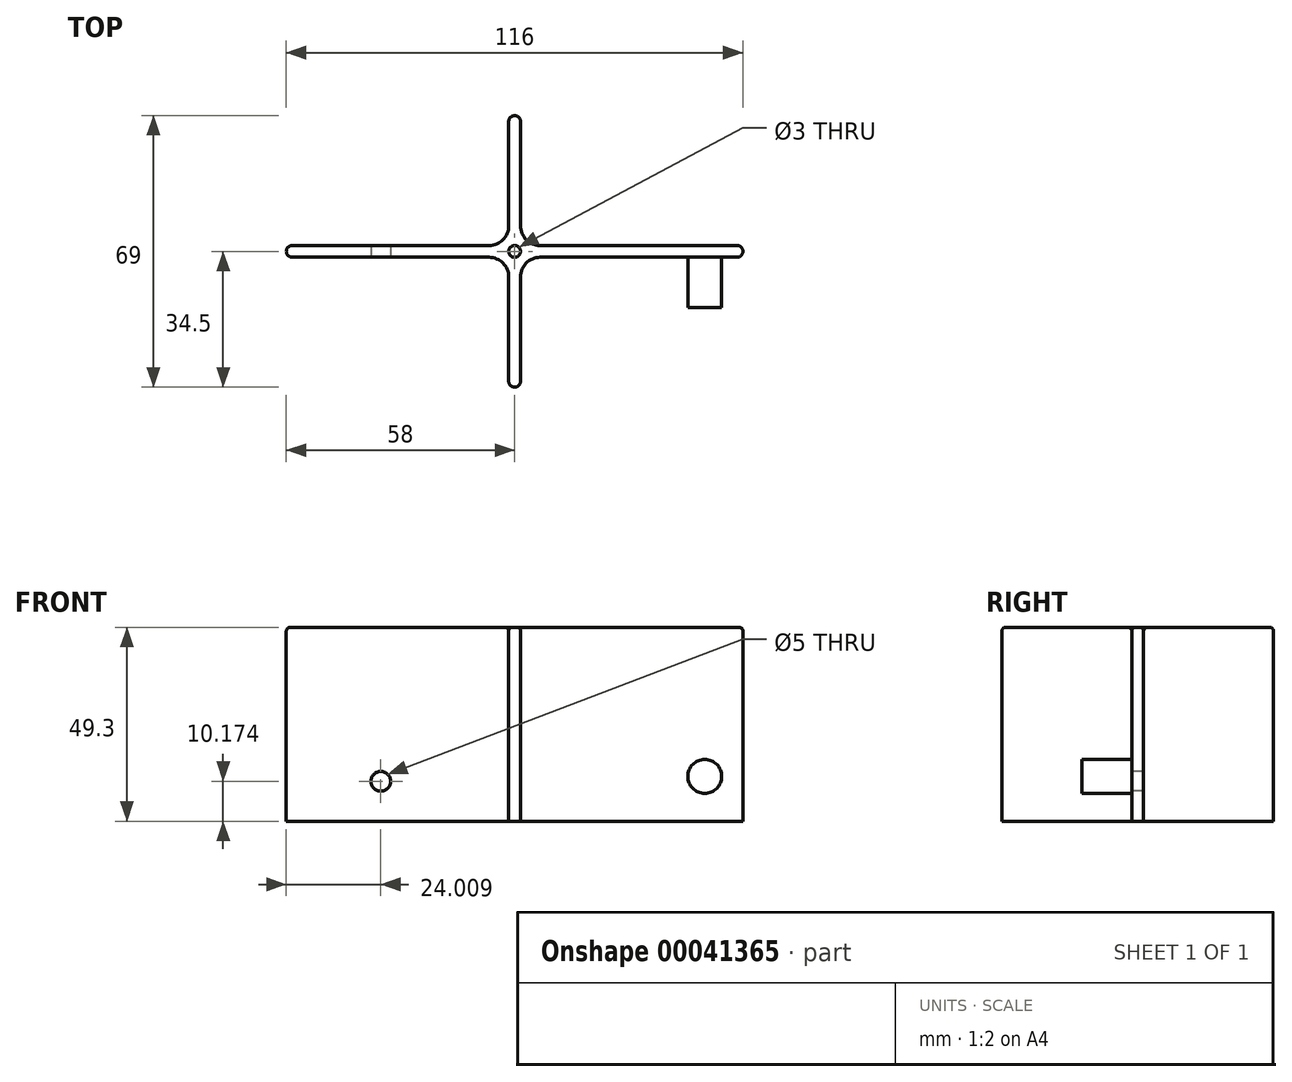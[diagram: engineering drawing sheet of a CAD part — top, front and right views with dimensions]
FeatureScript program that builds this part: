
annotation { "Feature Type Name" : "Feature", "Feature Type Description" : "" }
export const myFeature = defineFeature(function(context is Context, id is Id, definition is map)
    precondition{}
    {
        {
            var Q0;
            Q0=qCreatedBy(makeId("Top.planeOp"),FACE);
            var sketch = newSketch(context, id + "F0", { "sketchPlane" : qUnion([Q0])});
            skArc(sketch, "E0.0.startCap", {"start": v(0, -1.5) * mm, "mid": v(-1.5, 0) * mm, "end": v(0, 1.5) * mm});
            skArc(sketch, "E0.0.endCap", {"start": v(113, 1.5) * mm, "mid": v(114.5, 0) * mm, "end": v(113, -1.5) * mm});
            skLineSegment(sketch, "E0.0.left", {"start": v(0, 1.5) * mm, "end": v(55, 1.5) * mm});
            skLineSegment(sketch, "E0.0.right", {"start": v(0, -1.5) * mm, "end": v(55, -1.5) * mm});
            skArc(sketch, "E0.1.startCap", {"start": v(55, 33) * mm, "mid": v(56.5, 34.5) * mm, "end": v(58, 33) * mm});
            skArc(sketch, "E0.1.endCap", {"start": v(58, -33) * mm, "mid": v(56.5, -34.5) * mm, "end": v(55, -33) * mm});
            skLineSegment(sketch, "E0.1.left", {"start": v(58, 33) * mm, "end": v(58, 1.5) * mm});
            skLineSegment(sketch, "E0.1.right", {"start": v(55, 33) * mm, "end": v(55, 1.5) * mm});
            skLineSegment(sketch, "E1.trimOffspring", {"start": v(58, 1.5) * mm, "end": v(113, 1.5) * mm});
            skLineSegment(sketch, "E2.trimOffspring", {"start": v(58, -1.5) * mm, "end": v(58, -33) * mm});
            skLineSegment(sketch, "E3.trimOffspring", {"start": v(55, -1.5) * mm, "end": v(55, -33) * mm});
            skLineSegment(sketch, "E4.trimOffspring", {"start": v(58, -1.5) * mm, "end": v(113, -1.5) * mm});
            skSolve(sketch);
        }
        {
            var Q0;
            Q0 = qSketchRegion(id + "F0", true);
            extrude(context, id + "F1", {"entities" : qUnion([Q0]), "offsetDistance" : 25 * mm, "depth" : 49.3 * mm});
        }
        {
            var Q0;
            Q0=makeQuery(id+"F1.opExtrude","SWEPT_EDGE",EDGE,{"disambiguationData":[OSD([sQuery(id+"F0.wireOp",EDGE,"E2.trimOffspring"),sQuery(id+"F0.wireOp",EDGE,"E4.trimOffspring")])]});
            var Q1;
            Q1=makeQuery(id+"F1.opExtrude","SWEPT_EDGE",EDGE,{"disambiguationData":[OSD([sQuery(id+"F0.wireOp",EDGE,"E0.0.right"),sQuery(id+"F0.wireOp",EDGE,"E3.trimOffspring")])]});
            var Q2;
            Q2=makeQuery(id+"F1.opExtrude","SWEPT_EDGE",EDGE,{"disambiguationData":[OSD([sQuery(id+"F0.wireOp",EDGE,"E0.0.left"),sQuery(id+"F0.wireOp",EDGE,"E0.1.right")])]});
            var Q3;
            Q3=makeQuery(id+"F1.opExtrude","SWEPT_EDGE",EDGE,{"disambiguationData":[OSD([sQuery(id+"F0.wireOp",EDGE,"E0.1.left"),sQuery(id+"F0.wireOp",EDGE,"E1.trimOffspring")])]});
            fillet(context, id + "F2", {"entities" : qUnion([Q0, Q1, Q2, Q3]), "radius" : 5 * mm, "tangentPropagation" : true, "allowEdgeOverflow" : false});
        }
        {
            var Q0;
            Q0=makeQuery(id+"F1.opExtrude","CAP_FACE",FACE,{"disambiguationData":[OSD([sQuery(id+"F0.wireOp",EDGE,"E0.0.startCap"),sQuery(id+"F0.wireOp",EDGE,"E0.0.endCap"),sQuery(id+"F0.wireOp",EDGE,"E0.0.left"),sQuery(id+"F0.wireOp",EDGE,"E0.0.right"),sQuery(id+"F0.wireOp",EDGE,"E0.1.startCap"),sQuery(id+"F0.wireOp",EDGE,"E0.1.endCap"),sQuery(id+"F0.wireOp",EDGE,"E0.1.left"),sQuery(id+"F0.wireOp",EDGE,"E0.1.right"),sQuery(id+"F0.wireOp",EDGE,"E1.trimOffspring"),sQuery(id+"F0.wireOp",EDGE,"E2.trimOffspring"),sQuery(id+"F0.wireOp",EDGE,"E3.trimOffspring"),sQuery(id+"F0.wireOp",EDGE,"E4.trimOffspring")])],"isStart":false});
            var sketch = newSketch(context, id + "F3", { "sketchPlane" : qUnion([Q0])});
            skPoint(sketch, "E5", {"position": v(56.5, 0) * mm});
            skPoint(sketch, "E5.positionSnap0", {"position": v(56.5, -34.5) * mm});
            skSolve(sketch);
        }
        {
            var Q0;
            Q0=sQuery(id+"F3.wireOp",VERTEX,"E5");
            var Q1;
            Q1=makeQuery(id+"F1.opExtrude","SWEPT_BODY",BODY,{"disambiguationData":[OSD([sQuery(id+"F0.wireOp",EDGE,"E0.0.startCap"),sQuery(id+"F0.wireOp",EDGE,"E0.0.endCap"),sQuery(id+"F0.wireOp",EDGE,"E0.0.left"),sQuery(id+"F0.wireOp",EDGE,"E0.0.right"),sQuery(id+"F0.wireOp",EDGE,"E0.1.startCap"),sQuery(id+"F0.wireOp",EDGE,"E0.1.endCap"),sQuery(id+"F0.wireOp",EDGE,"E0.1.left"),sQuery(id+"F0.wireOp",EDGE,"E0.1.right"),sQuery(id+"F0.wireOp",EDGE,"E1.trimOffspring"),sQuery(id+"F0.wireOp",EDGE,"E2.trimOffspring"),sQuery(id+"F0.wireOp",EDGE,"E3.trimOffspring"),sQuery(id+"F0.wireOp",EDGE,"E4.trimOffspring")])]});
            hole(context, id + "F4", {"style" : HoleStyle.SIMPLE, "holeDiameter" : 3 * mm, "endStyle" : HoleEndStyle.THROUGH, "locations" : qUnion([Q0]), "scope" : qUnion([Q1])});
        }
        {
            var Q0;
            Q0=makeQuery(id+"F1.opExtrude","CAP_FACE",FACE,{"disambiguationData":[OSD([sQuery(id+"F0.wireOp",EDGE,"E0.0.startCap"),sQuery(id+"F0.wireOp",EDGE,"E0.0.endCap"),sQuery(id+"F0.wireOp",EDGE,"E0.0.left"),sQuery(id+"F0.wireOp",EDGE,"E0.0.right"),sQuery(id+"F0.wireOp",EDGE,"E0.1.startCap"),sQuery(id+"F0.wireOp",EDGE,"E0.1.endCap"),sQuery(id+"F0.wireOp",EDGE,"E0.1.left"),sQuery(id+"F0.wireOp",EDGE,"E0.1.right"),sQuery(id+"F0.wireOp",EDGE,"E1.trimOffspring"),sQuery(id+"F0.wireOp",EDGE,"E2.trimOffspring"),sQuery(id+"F0.wireOp",EDGE,"E3.trimOffspring"),sQuery(id+"F0.wireOp",EDGE,"E4.trimOffspring")])],"isStart":false});
            fillet(context, id + "F5", {"entities" : qUnion([Q0]), "radius" : 1 * mm, "tangentPropagation" : true, "allowEdgeOverflow" : false});
        }
        {
            var Q0;
            Q0=makeQuery(id+"F1.opExtrude","SWEPT_FACE",FACE,{"disambiguationData":[OSD([sQuery(id+"F0.wireOp",EDGE,"E1.trimOffspring")])]});
            var sketch = newSketch(context, id + "F6", { "sketchPlane" : qUnion([Q0])});
            skCircle(sketch, "E6", {"center": v(-104.81, 11.42) * mm, "radius": 4.3 * mm});
            skSolve(sketch);
        }
        {
            var Q0;
            Q0=makeQuery(id+"F6.imprint","IMPRINT",FACE,{"disambiguationData":[TD([[makeQuery(id+"F6.imprint","IMPRINT",EDGE,{"derivedFrom":sQuery(id+"F6.wireOp",EDGE,"E6")}),1.0]])]});
            extrude(context, id + "F7", {"entities" : qUnion([Q0]), "operationType" : NewBodyOperationType.ADD, "oppositeDirection" : true, "depth" : 15.71 * mm});
        }
        {
            var Q0;
            Q0=makeQuery(id+"F1.opExtrude","SWEPT_FACE",FACE,{"disambiguationData":[OSD([sQuery(id+"F0.wireOp",EDGE,"E0.0.right")])]});
            var sketch = newSketch(context, id + "F9", { "sketchPlane" : qUnion([Q0])});
            skPoint(sketch, "E7", {"position": v(22.5, 10.17) * mm});
            skPoint(sketch, "E8", {"position": v(7.6, 7.95) * mm});
            skSolve(sketch);
        }
        {
            var Q0;
            Q0=sQuery(id+"F9.wireOp",VERTEX,"E7");
            var Q1;
            Q1=makeQuery(id+"F1.opExtrude","SWEPT_BODY",BODY,{"disambiguationData":[OSD([sQuery(id+"F0.wireOp",EDGE,"E0.0.startCap"),sQuery(id+"F0.wireOp",EDGE,"E0.0.endCap"),sQuery(id+"F0.wireOp",EDGE,"E0.0.left"),sQuery(id+"F0.wireOp",EDGE,"E0.0.right"),sQuery(id+"F0.wireOp",EDGE,"E0.1.startCap"),sQuery(id+"F0.wireOp",EDGE,"E0.1.endCap"),sQuery(id+"F0.wireOp",EDGE,"E0.1.left"),sQuery(id+"F0.wireOp",EDGE,"E0.1.right"),sQuery(id+"F0.wireOp",EDGE,"E1.trimOffspring"),sQuery(id+"F0.wireOp",EDGE,"E2.trimOffspring"),sQuery(id+"F0.wireOp",EDGE,"E3.trimOffspring"),sQuery(id+"F0.wireOp",EDGE,"E4.trimOffspring")])]});
            hole(context, id + "F8", {"style" : HoleStyle.SIMPLE, "endStyle" : HoleEndStyle.THROUGH, "holeDiameter" : 5 * mm, "locations" : qUnion([Q0]), "scope" : qUnion([Q1]), "isTappedThrough" : true});
        }
    });
